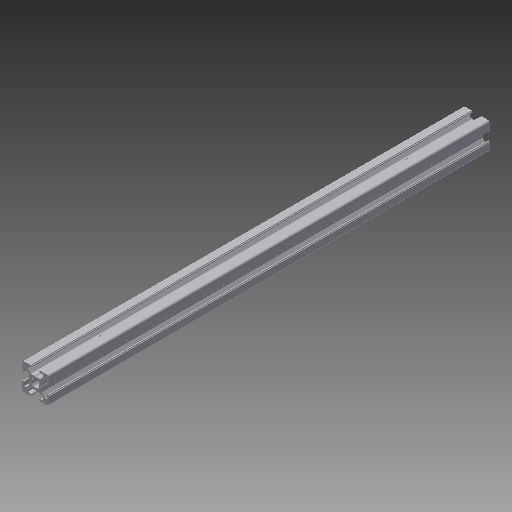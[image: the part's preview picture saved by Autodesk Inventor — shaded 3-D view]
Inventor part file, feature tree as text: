
AUTODESK INVENTOR PART (.ipt)
format: ipt  version: 2017 (Build 210142000, 142)  size: 407,040 bytes
history: native  units: in
note: dims shown in document units (in); Inventor stores cm internally (conversion verified against a paired STEP export)
features: other x3, sketch x2, extrude x1, hole x1, mirror x1
ambient origin geometry x8: Origin, YZ Plane, XZ Plane, XY Plane, X Axis, Y Axis, Z Axis, Center Point
bodies: Solid1 (feature_tree)
feature tree (8):
  other  "Blocks"
  extrude  "Extrusion1"  Depth=2.0in
  hole  "Hole1"  [1 undecoded]
  mirror  "Mirror1"
  sketch  "Sketch1"  dims[d1=0.0in d5=2.0in]
  other  "20x20"
  sketch  "Sketch3"  dims[d6=0.187in d7=0.75in d8=0.375in d9=0.25in d10=0.5635in d11=1.0in d12=0.8108in d13=1.0in d14=1.0in]
  other  "20x20:1"
note: 1 required parameter value undecoded (feature->parameter linkage not recoverable at this tier; creation-order binding heuristic only, values carry confidence <= 0.55)
